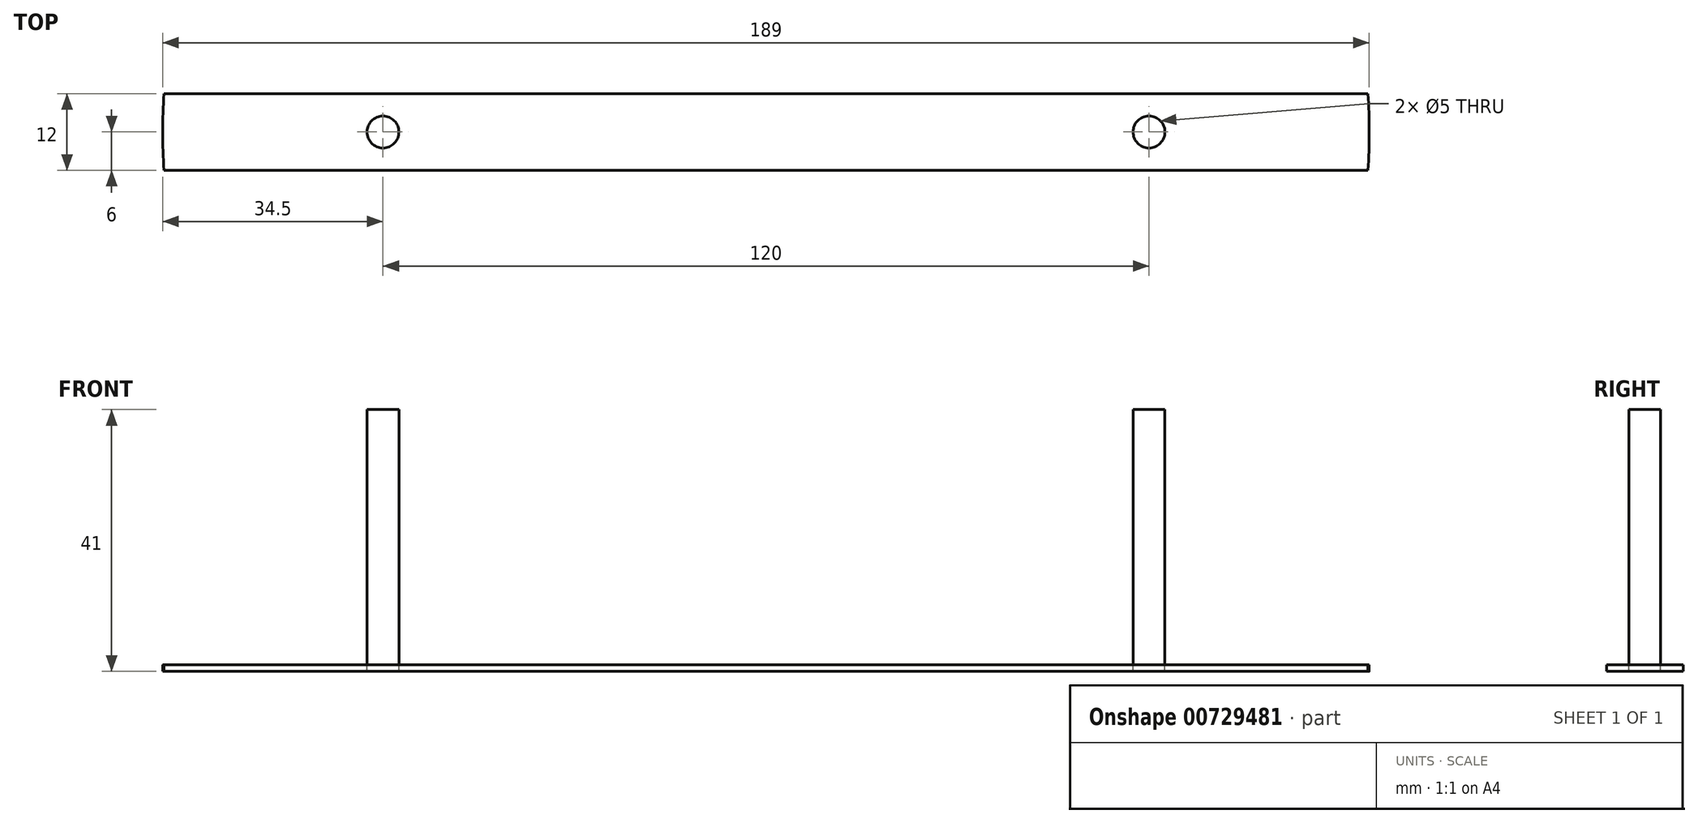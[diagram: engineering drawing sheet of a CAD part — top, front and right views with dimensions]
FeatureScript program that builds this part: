
annotation { "Feature Type Name" : "Feature", "Feature Type Description" : "" }
export const myFeature = defineFeature(function(context is Context, id is Id, definition is map)
    precondition{}
    {
        {
            var Q0;
            Q0=qCreatedBy(makeId("Top.planeOp"),FACE);
            var sketch = newSketch(context, id + "F0", { "sketchPlane" : qUnion([Q0])});
            skCircle(sketch, "E0", {"center": v(0, 0) * mm, "radius": 94.5 * mm});
            skLineSegment(sketch, "E1", {"start": v(-94.3, 6) * mm, "end": v(94.3, 6) * mm});
            skLineSegment(sketch, "E2", {"start": v(-94.3, -6) * mm, "end": v(94.3, -6) * mm});
            skPoint(sketch, "E3", {"position": v(60, 0) * mm});
            skPoint(sketch, "E4", {"position": v(-60, 0) * mm});
            skCircle(sketch, "E5", {"center": v(-60, 0) * mm, "radius": 2.5 * mm});
            skCircle(sketch, "E6", {"center": v(60, 0) * mm, "radius": 2.5 * mm});
            skSolve(sketch);
        }
        {
            var Q0;
            Q0=makeQuery(id+"F0.imprint","IMPRINT",FACE,{"disambiguationData":[TD([[makeQuery(id+"F0.imprint","IMPRINT",EDGE,{"derivedFrom":sQuery(id+"F0.wireOp",EDGE,"x2w9MEZl-GaG9-8zoM-PNZs-dDrqogZVktmc")}),1.0]])]});
            var Q1;
            Q1=makeQuery(id+"F0.imprint","IMPRINT",FACE,{"disambiguationData":[TD([[makeQuery(id+"F0.imprint","IMPRINT",EDGE,{"derivedFrom":sQuery(id+"F0.wireOp",EDGE,"E5")}),1.0]])]});
            var Q2;
            Q2=makeQuery(id+"F0.imprint","IMPRINT",FACE,{"disambiguationData":[TD([[makeQuery(id+"F0.imprint","IMPRINT",EDGE,{"derivedFrom":sQuery(id+"F0.wireOp",EDGE,"E6")}),1.0]])]});
            extrude(context, id + "F1", {"entities" : qUnion([Q0, Q1, Q2]), "depth" : 40 * mm, "offsetDistance" : 25 * mm});
        }
        {
            var Q0;
            Q0=makeQuery(id+"F0.imprint","IMPRINT",FACE,{"disambiguationData":[TD([[makeQuery(id+"F0.imprint","IMPRINT",EDGE,{"derivedFrom":sQuery(id+"F0.wireOp",EDGE,"x2w9MEZl-GaG9-8zoM-PNZs-dDrqogZVktmc")}),-1.0]])]});
            var Q1;
            {var subQ1=sQuery(id+"F0.wireOp",EDGE,"E1");Q1=makeQuery(id+"F0.imprint","IMPRINT",FACE,{"disambiguationData":[TD([[makeQuery(id+"F0.imprint","IMPRINT",EDGE,{"derivedFrom":subQ1}),-1.0]])]});}
            extrude(context, id + "F2", {"entities" : qUnion([Q0, Q1]), "oppositeDirection" : true, "depth" : 1 * mm, "offsetDistance" : 25 * mm});
        }
    });
